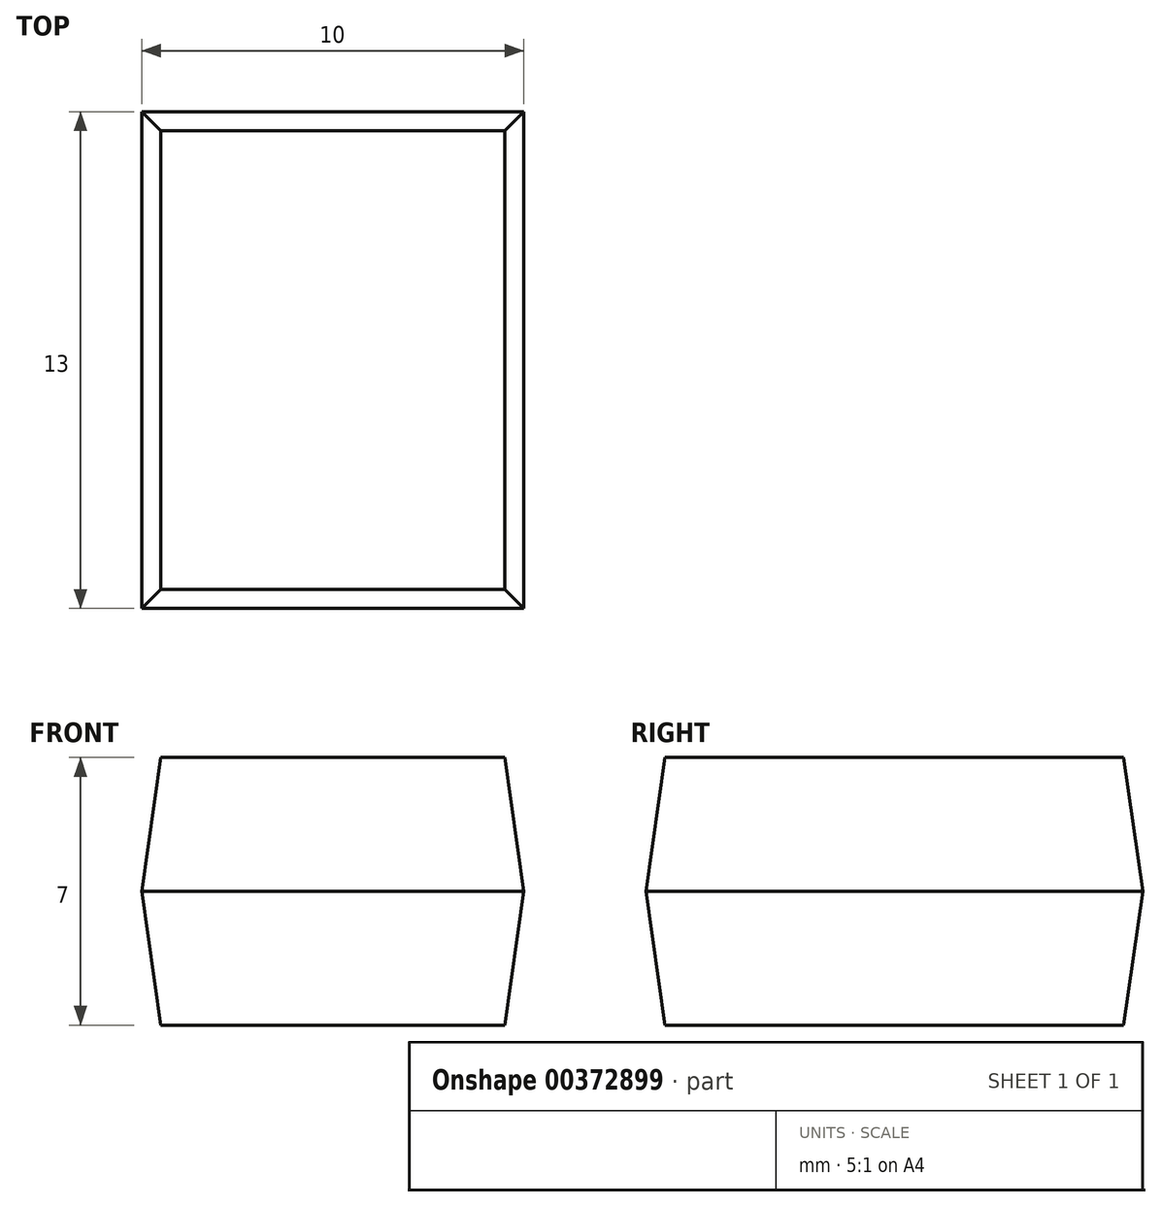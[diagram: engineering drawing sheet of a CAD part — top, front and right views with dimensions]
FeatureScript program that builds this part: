
annotation { "Feature Type Name" : "Feature", "Feature Type Description" : "" }
export const myFeature = defineFeature(function(context is Context, id is Id, definition is map)
    precondition{}
    {
        {
            var Q0;
            Q0=qCreatedBy(makeId("Top.planeOp"),FACE);
            var sketch = newSketch(context, id + "F0", { "sketchPlane" : qUnion([Q0])});
            skLineSegment(sketch, "E0.bottom", {"start": v(-5, -6.5) * mm, "end": v(5, -6.5) * mm});
            skLineSegment(sketch, "E0.top", {"start": v(-5, 6.5) * mm, "end": v(5, 6.5) * mm});
            skLineSegment(sketch, "E0.left", {"start": v(-5, -6.5) * mm, "end": v(-5, 6.5) * mm});
            skLineSegment(sketch, "E0.right", {"start": v(5, -6.5) * mm, "end": v(5, 6.5) * mm});
            skSolve(sketch);
        }
        {
            var Q0;
            Q0=makeQuery(id+"F0.imprint","IMPRINT",FACE,{"disambiguationData":[TD([[makeQuery(id+"F0.imprint","IMPRINT",EDGE,{"derivedFrom":sQuery(id+"F0.wireOp",EDGE,"E0.bottom")}),1.0]])]});
            extrude(context, id + "F1", {"entities" : qUnion([Q0]), "depth" : 7 * mm});
        }
        {
            var Q0;
            Q0=makeQuery(id+"F1.opExtrude","CAP_FACE",FACE,{"disambiguationData":[OSD([sQuery(id+"F0.wireOp",EDGE,"E0.bottom"),sQuery(id+"F0.wireOp",EDGE,"E0.top"),sQuery(id+"F0.wireOp",EDGE,"E0.left"),sQuery(id+"F0.wireOp",EDGE,"E0.right")])],"isStart":false});
            chamfer(context, id + "F2", {"entities" : qUnion([Q0]), "chamferType" : ChamferType.TWO_OFFSETS, "width1" : 0.5 * mm, "oppositeDirection" : false, "width2" : 3.5 * mm, "tangentPropagation" : true});
        }
        {
            var Q0;
            Q0=makeQuery(id+"F1.opExtrude","CAP_FACE",FACE,{"disambiguationData":[OSD([sQuery(id+"F0.wireOp",EDGE,"E0.bottom"),sQuery(id+"F0.wireOp",EDGE,"E0.top"),sQuery(id+"F0.wireOp",EDGE,"E0.left"),sQuery(id+"F0.wireOp",EDGE,"E0.right")])],"isStart":true});
            chamfer(context, id + "F3", {"entities" : qUnion([Q0]), "chamferType" : ChamferType.TWO_OFFSETS, "width1" : 3.5 * mm, "oppositeDirection" : false, "width2" : 0.5 * mm, "tangentPropagation" : true});
        }
    });
